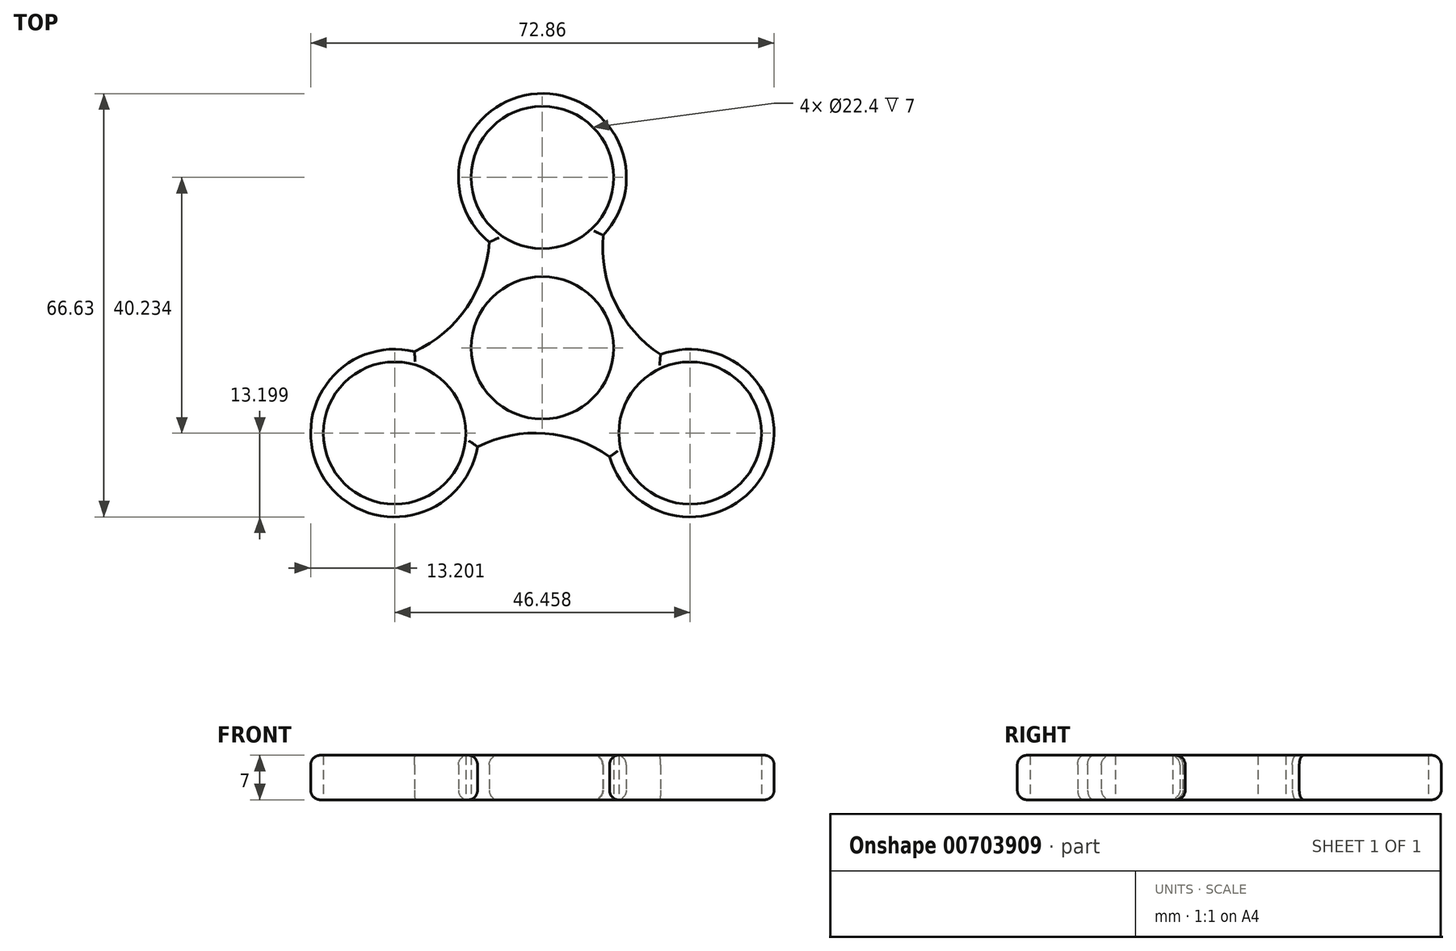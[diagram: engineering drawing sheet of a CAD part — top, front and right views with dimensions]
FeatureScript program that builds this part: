
annotation { "Feature Type Name" : "Feature", "Feature Type Description" : "" }
export const myFeature = defineFeature(function(context is Context, id is Id, definition is map)
    precondition{}
    {
        {
            var Q0;
            Q0=qCreatedBy(makeId("Top.planeOp"),FACE);
            var sketch = newSketch(context, id + "F0", { "sketchPlane" : qUnion([Q0])});
            skCircle(sketch, "E0", {"center": v(0, 0) * mm, "radius": 11.2 * mm});
            skCircle(sketch, "E1", {"center": v(0, 26.82) * mm, "radius": 11.2 * mm});
            skArc(sketch, "E2", {"start": v(9.56, 17.72) * mm, "mid": v(-0.8, 40) * mm, "end": v(-8.38, 16.62) * mm});
            skArc(sketch, "E3.1.0", {"start": v(-20.12, -0.58) * mm, "mid": v(-34.24, -20.7) * mm, "end": v(-10.2, -15.56) * mm});
            skCircle(sketch, "E3.1.1", {"center": v(-23.23, -13.41) * mm, "radius": 11.2 * mm});
            skArc(sketch, "E3.2.0", {"start": v(10.57, -17.13) * mm, "mid": v(35.04, -19.3) * mm, "end": v(18.58, -1.06) * mm});
            skCircle(sketch, "E3.2.1", {"center": v(23.23, -13.41) * mm, "radius": 11.2 * mm});
            skArc(sketch, "E4", {"start": v(9.56, 17.72) * mm, "mid": v(11.46, 7.08) * mm, "end": v(18.58, -1.06) * mm});
            skArc(sketch, "E5.1.0", {"start": v(-20.12, -0.58) * mm, "mid": v(-11.86, 6.39) * mm, "end": v(-8.38, 16.62) * mm});
            skArc(sketch, "E5.2.0", {"start": v(10.57, -17.13) * mm, "mid": v(0.4, -13.46) * mm, "end": v(-10.2, -15.56) * mm});
            skSolve(sketch);
        }
        {
            var Q0;
            Q0 = qSketchRegion(id + "F0", true);
            extrude(context, id + "F1", {"entities" : qUnion([Q0]), "depth" : 7 * mm, "offsetDistance" : 25 * mm});
        }
        {
            var Q0;
            Q0=makeQuery(id+"F1.opExtrude","CAP_EDGE",EDGE,{"disambiguationData":[OSD([sQuery(id+"F0.wireOp",EDGE,"E4")])],"isStart":false});
            var Q1;
            Q1=makeQuery(id+"F1.opExtrude","CAP_EDGE",EDGE,{"disambiguationData":[OSD([sQuery(id+"F0.wireOp",EDGE,"E3.2.0")])],"isStart":false});
            var Q2;
            Q2=makeQuery(id+"F1.opExtrude","CAP_EDGE",EDGE,{"disambiguationData":[OSD([sQuery(id+"F0.wireOp",EDGE,"E5.2.0")])],"isStart":false});
            var Q3;
            Q3=makeQuery(id+"F1.opExtrude","CAP_EDGE",EDGE,{"disambiguationData":[OSD([sQuery(id+"F0.wireOp",EDGE,"E3.1.0")])],"isStart":false});
            var Q4;
            Q4=makeQuery(id+"F1.opExtrude","CAP_EDGE",EDGE,{"disambiguationData":[OSD([sQuery(id+"F0.wireOp",EDGE,"E5.1.0")])],"isStart":false});
            var Q5;
            Q5=makeQuery(id+"F1.opExtrude","CAP_EDGE",EDGE,{"disambiguationData":[OSD([sQuery(id+"F0.wireOp",EDGE,"E2")])],"isStart":false});
            fillet(context, id + "F2", {"entities" : qUnion([Q0, Q1, Q2, Q3, Q4, Q5]), "radius" : 1.5 * mm, "tangentPropagation" : true, "allowEdgeOverflow" : false});
        }
        {
            var Q0;
            Q0=makeQuery(id+"F1.opExtrude","CAP_EDGE",EDGE,{"disambiguationData":[OSD([sQuery(id+"F0.wireOp",EDGE,"E3.1.0")])],"isStart":true});
            var Q1;
            Q1=makeQuery(id+"F1.opExtrude","CAP_EDGE",EDGE,{"disambiguationData":[OSD([sQuery(id+"F0.wireOp",EDGE,"E5.2.0")])],"isStart":true});
            var Q2;
            Q2=makeQuery(id+"F1.opExtrude","CAP_EDGE",EDGE,{"disambiguationData":[OSD([sQuery(id+"F0.wireOp",EDGE,"E5.1.0")])],"isStart":true});
            var Q3;
            Q3=makeQuery(id+"F1.opExtrude","CAP_EDGE",EDGE,{"disambiguationData":[OSD([sQuery(id+"F0.wireOp",EDGE,"E2")])],"isStart":true});
            var Q4;
            Q4=makeQuery(id+"F1.opExtrude","CAP_EDGE",EDGE,{"disambiguationData":[OSD([sQuery(id+"F0.wireOp",EDGE,"E4")])],"isStart":true});
            var Q5;
            Q5=makeQuery(id+"F1.opExtrude","CAP_EDGE",EDGE,{"disambiguationData":[OSD([sQuery(id+"F0.wireOp",EDGE,"E3.2.0")])],"isStart":true});
            fillet(context, id + "F3", {"entities" : qUnion([Q0, Q1, Q2, Q3, Q4, Q5]), "radius" : 1.5 * mm, "tangentPropagation" : true, "allowEdgeOverflow" : false});
        }
    });
